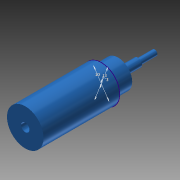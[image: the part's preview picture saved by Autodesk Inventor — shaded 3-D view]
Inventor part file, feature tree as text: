
AUTODESK INVENTOR PART (.ipt)
format: ipt  version: 2013 SP2 (Build 170200200, 200)  size: 94,208 bytes
history: native  units: in
note: dims shown in document units (in); Inventor stores cm internally (conversion verified against a paired STEP export)
features: extrude x4, sketch x2
ambient origin geometry x8: Origin, YZ Plane, XZ Plane, XY Plane, X Axis, Y Axis, Z Axis, Center Point
bodies: Solid1 (feature_tree)
feature tree (6):
  sketch  "Sketch1"  dims[d5=1.063in d6=0.0in d11=0.5118in]
  extrude  "Extrusion1"  Depth=0.5118in
  extrude  "Extrusion3"  Depth=0.1181in
  extrude  "Extrusion4"  Depth=0.2362in TaperAngle=0.0deg
  extrude  "Extrusion5"  Depth=0.5118in TaperAngle=0.0deg
  sketch  "Sketch3"  dims[d12=0.3937in d13=0.1181in d14=0.2362in d15=0.0in d16=0.5118in d17=0.0in d18=0.0787in d19=0.2362in d20=0.0in]
